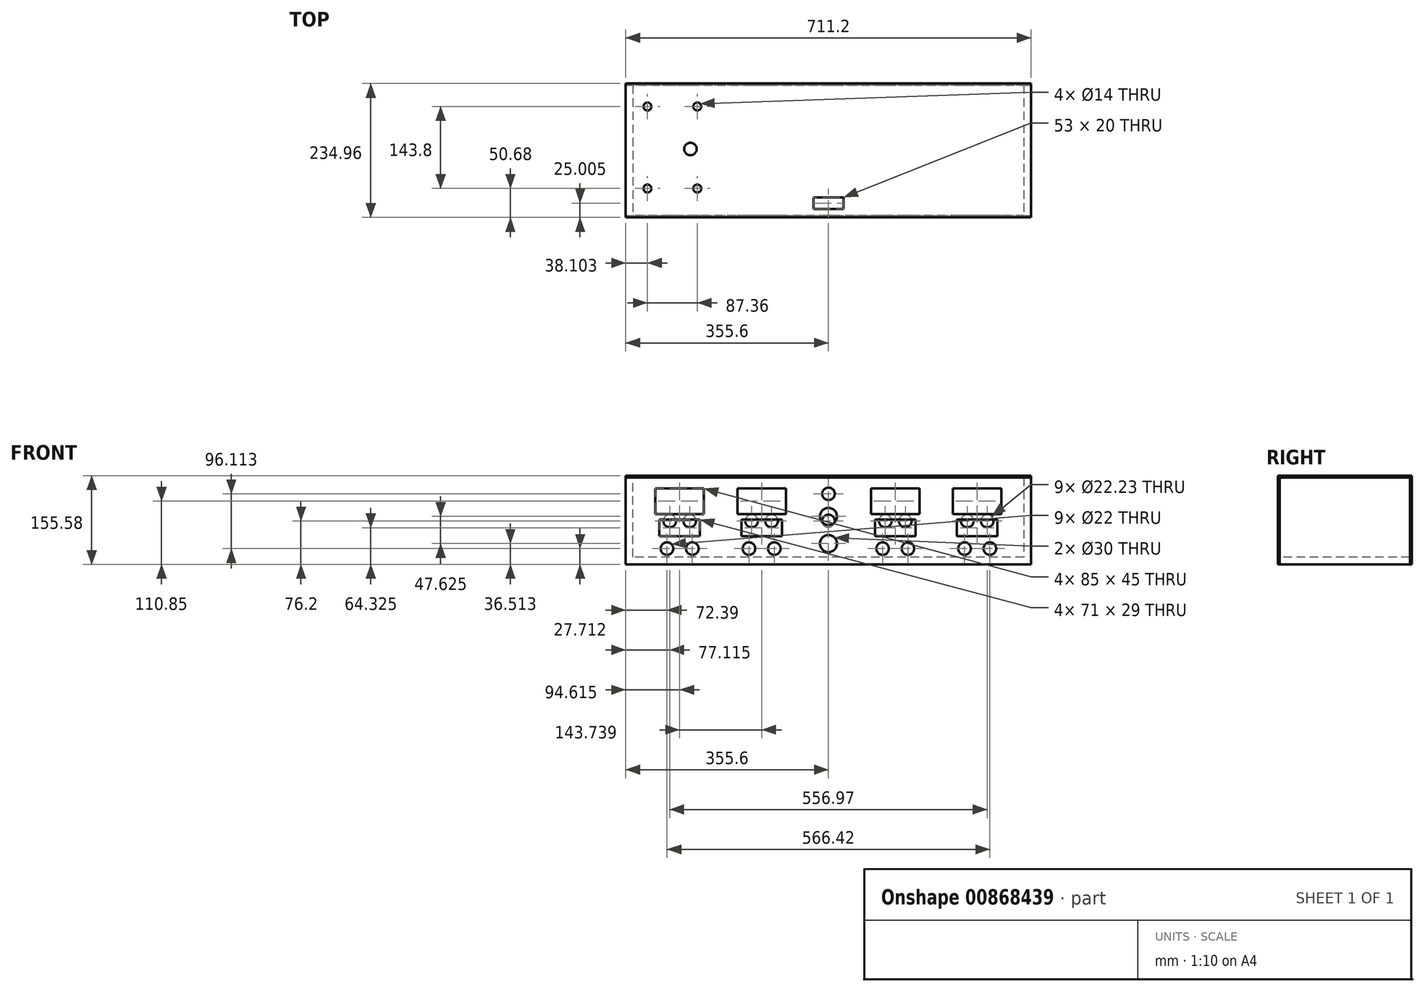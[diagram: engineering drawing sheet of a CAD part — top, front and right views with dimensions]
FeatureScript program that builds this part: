
annotation { "Feature Type Name" : "Feature", "Feature Type Description" : "" }
export const myFeature = defineFeature(function(context is Context, id is Id, definition is map)
    precondition{}
    {
        {
            var Q0;
            Q0=qCreatedBy(makeId("Front.planeOp"),FACE);
            var sketch = newSketch(context, id + "F0", { "sketchPlane" : qUnion([Q0])});
            skLineSegment(sketch, "E0.bottom", {"start": v(0, 0) * mm, "end": v(711.2, 0) * mm});
            skLineSegment(sketch, "E0.top", {"start": v(0, 152.4) * mm, "end": v(711.2, 152.4) * mm});
            skLineSegment(sketch, "E0.left", {"start": v(0, 0) * mm, "end": v(0, 152.4) * mm});
            skLineSegment(sketch, "E0.right", {"start": v(711.2, 0) * mm, "end": v(711.2, 152.4) * mm});
            skLineSegment(sketch, "E1.bottom", {"start": v(52.11, 133.35) * mm, "end": v(137.11, 133.35) * mm});
            skLineSegment(sketch, "E1.top", {"start": v(52.11, 88.35) * mm, "end": v(137.11, 88.35) * mm});
            skLineSegment(sketch, "E1.left", {"start": v(52.11, 133.35) * mm, "end": v(52.11, 88.35) * mm});
            skLineSegment(sketch, "E1.right", {"start": v(137.11, 133.35) * mm, "end": v(137.11, 88.35) * mm});
            skLineSegment(sketch, "E2.bottom", {"start": v(59.11, 78.83) * mm, "end": v(130.11, 78.83) * mm});
            skLineSegment(sketch, "E2.top", {"start": v(59.11, 49.83) * mm, "end": v(130.11, 49.83) * mm});
            skLineSegment(sketch, "E2.left", {"start": v(59.11, 78.83) * mm, "end": v(59.11, 49.83) * mm});
            skLineSegment(sketch, "E2.right", {"start": v(130.11, 78.83) * mm, "end": v(130.11, 49.83) * mm});
            skPoint(sketch, "E3", {"position": v(94.61, 133.35) * mm});
            skPoint(sketch, "E4", {"position": v(94.61, 88.35) * mm});
            skPoint(sketch, "E5", {"position": v(94.61, 78.83) * mm});
            skPoint(sketch, "E6", {"position": v(94.61, 49.83) * mm});
            skLineSegment(sketch, "E7", {"start": v(0, 139.7) * mm, "end": v(711.2, 139.7) * mm, "construction": true});
            skLineSegment(sketch, "E8", {"start": v(711.2, 12.7) * mm, "end": v(0, 12.7) * mm});
            skLineSegment(sketch, "E9", {"start": v(12.7, 0) * mm, "end": v(12.7, 152.4) * mm});
            skLineSegment(sketch, "E10", {"start": v(698.5, 152.4) * mm, "end": v(698.5, 0) * mm});
            skLineSegment(sketch, "E11", {"start": v(94.61, 139.7) * mm, "end": v(94.61, 12.7) * mm, "construction": true});
            skCircle(sketch, "E12", {"center": v(72.39, 27.71) * mm, "radius": 11 * mm});
            skCircle(sketch, "E13", {"center": v(116.84, 27.71) * mm, "radius": 11 * mm});
            skLineSegment(sketch, "E14", {"start": v(72.39, 27.71) * mm, "end": v(116.84, 27.71) * mm, "construction": true});
            skPoint(sketch, "E15", {"position": v(94.61, 27.71) * mm});
            skLineSegment(sketch, "E16.0", {"start": v(49.11, 136.35) * mm, "end": v(49.11, 85.35) * mm, "construction": true});
            skLineSegment(sketch, "E16.1", {"start": v(49.12, 136.35) * mm, "end": v(140.11, 136.35) * mm, "construction": true});
            skLineSegment(sketch, "E16.2", {"start": v(140.12, 136.35) * mm, "end": v(140.11, 85.35) * mm, "construction": true});
            skLineSegment(sketch, "E16.3", {"start": v(49.11, 85.35) * mm, "end": v(140.11, 85.35) * mm, "construction": true});
            skLineSegment(sketch, "E17.0", {"start": v(55.11, 82.83) * mm, "end": v(134.11, 82.83) * mm, "construction": true});
            skLineSegment(sketch, "E17.1", {"start": v(55.11, 82.83) * mm, "end": v(55.11, 45.83) * mm, "construction": true});
            skLineSegment(sketch, "E17.2", {"start": v(55.11, 45.83) * mm, "end": v(134.11, 45.83) * mm, "construction": true});
            skLineSegment(sketch, "E17.3", {"start": v(134.11, 82.83) * mm, "end": v(134.11, 45.83) * mm, "construction": true});
            skCircle(sketch, "E18.0", {"center": v(72.39, 27.71) * mm, "radius": 15 * mm, "construction": true});
            skCircle(sketch, "E19.0", {"center": v(116.84, 27.71) * mm, "radius": 15 * mm, "construction": true});
            skLineSegment(sketch, "E20", {"start": v(616.59, 139.7) * mm, "end": v(616.59, 12.7) * mm, "construction": true});
            skLineSegment(sketch, "E21", {"start": v(355.6, 139.7) * mm, "end": v(355.6, 12.7) * mm, "construction": true});
            skLineSegment(sketch, "E22", {"start": v(238.35, 139.7) * mm, "end": v(238.35, 12.7) * mm, "construction": true});
            skLineSegment(sketch, "E23", {"start": v(472.85, 139.7) * mm, "end": v(472.85, 12.7) * mm, "construction": true});
            skLineSegment(sketch, "E24", {"start": v(166.48, 152.4) * mm, "end": v(166.48, 0) * mm, "construction": true});
            skLineSegment(sketch, "E25", {"start": v(544.72, 152.4) * mm, "end": v(544.72, 0) * mm, "construction": true});
            skLineSegment(sketch, "E26.MirrorCS", {"start": v(280.85, 133.35) * mm, "end": v(195.85, 133.35) * mm});
            skLineSegment(sketch, "E27.MirrorCS", {"start": v(192.85, 136.35) * mm, "end": v(192.85, 85.35) * mm, "construction": true});
            skLineSegment(sketch, "E28.MirrorCS", {"start": v(280.85, 133.35) * mm, "end": v(280.85, 88.35) * mm});
            skLineSegment(sketch, "E29.MirrorCS", {"start": v(277.85, 82.83) * mm, "end": v(277.85, 45.83) * mm, "construction": true});
            skLineSegment(sketch, "E30.MirrorCS", {"start": v(273.85, 78.83) * mm, "end": v(202.85, 78.83) * mm});
            skLineSegment(sketch, "E31.MirrorCS", {"start": v(280.85, 88.35) * mm, "end": v(195.85, 88.35) * mm});
            skLineSegment(sketch, "E32.MirrorCS", {"start": v(260.58, 27.71) * mm, "end": v(216.13, 27.71) * mm, "construction": true});
            skPoint(sketch, "E33.MirrorP", {"position": v(238.35, 27.71) * mm});
            skLineSegment(sketch, "E34.MirrorCS", {"start": v(195.85, 133.35) * mm, "end": v(195.85, 88.35) * mm});
            skCircle(sketch, "E35.MirrorC", {"center": v(216.13, 27.71) * mm, "radius": 11 * mm});
            skLineSegment(sketch, "E36.MirrorCS", {"start": v(283.85, 85.35) * mm, "end": v(192.85, 85.35) * mm, "construction": true});
            skPoint(sketch, "E37.MirrorP", {"position": v(238.35, 133.35) * mm});
            skCircle(sketch, "E38.MirrorC", {"center": v(260.58, 27.71) * mm, "radius": 11 * mm});
            skLineSegment(sketch, "E39.MirrorCS", {"start": v(273.85, 49.83) * mm, "end": v(202.85, 49.83) * mm});
            skLineSegment(sketch, "E40.MirrorCS", {"start": v(277.85, 45.83) * mm, "end": v(198.85, 45.83) * mm, "construction": true});
            skPoint(sketch, "E41.MirrorP", {"position": v(238.35, 78.83) * mm});
            skPoint(sketch, "E42.MirrorP", {"position": v(238.35, 49.83) * mm});
            skLineSegment(sketch, "E43.MirrorCS", {"start": v(273.85, 78.83) * mm, "end": v(273.85, 49.83) * mm});
            skPoint(sketch, "E44.MirrorP", {"position": v(238.35, 88.35) * mm});
            skLineSegment(sketch, "E45.MirrorCS", {"start": v(198.85, 82.83) * mm, "end": v(198.85, 45.83) * mm, "construction": true});
            skLineSegment(sketch, "E46.MirrorCS", {"start": v(277.85, 82.83) * mm, "end": v(198.85, 82.83) * mm, "construction": true});
            skLineSegment(sketch, "E47.MirrorCS", {"start": v(283.85, 136.35) * mm, "end": v(192.85, 136.35) * mm, "construction": true});
            skLineSegment(sketch, "E48.MirrorCS", {"start": v(283.85, 136.35) * mm, "end": v(283.85, 85.35) * mm, "construction": true});
            skLineSegment(sketch, "E49.MirrorCS", {"start": v(202.85, 78.83) * mm, "end": v(202.85, 49.83) * mm});
            skCircle(sketch, "E50.MirrorC", {"center": v(216.13, 27.71) * mm, "radius": 15 * mm, "construction": true});
            skCircle(sketch, "E51.MirrorC", {"center": v(260.58, 27.71) * mm, "radius": 15 * mm, "construction": true});
            skLineSegment(sketch, "E52.MirrorCS", {"start": v(430.35, 88.35) * mm, "end": v(515.35, 88.35) * mm});
            skLineSegment(sketch, "E53.MirrorCS", {"start": v(518.35, 136.35) * mm, "end": v(518.35, 85.35) * mm, "construction": true});
            skLineSegment(sketch, "E54.MirrorCS", {"start": v(656.09, 45.83) * mm, "end": v(577.09, 45.83) * mm, "construction": true});
            skLineSegment(sketch, "E55.MirrorCS", {"start": v(515.35, 133.35) * mm, "end": v(515.35, 88.35) * mm});
            skLineSegment(sketch, "E56.MirrorCS", {"start": v(656.09, 82.83) * mm, "end": v(656.09, 45.83) * mm, "construction": true});
            skCircle(sketch, "E57.MirrorC", {"center": v(450.62, 27.71) * mm, "radius": 11 * mm});
            skPoint(sketch, "E58.MirrorP", {"position": v(472.85, 88.35) * mm});
            skPoint(sketch, "E59.MirrorP", {"position": v(616.59, 78.83) * mm});
            skLineSegment(sketch, "E60.MirrorCS", {"start": v(574.09, 133.35) * mm, "end": v(574.09, 88.35) * mm});
            skLineSegment(sketch, "E61.MirrorCS", {"start": v(433.35, 82.83) * mm, "end": v(512.35, 82.83) * mm, "construction": true});
            skLineSegment(sketch, "E62.MirrorCS", {"start": v(662.09, 136.35) * mm, "end": v(571.09, 136.35) * mm, "construction": true});
            skLineSegment(sketch, "E63.MirrorCS", {"start": v(437.35, 49.83) * mm, "end": v(508.35, 49.83) * mm});
            skPoint(sketch, "E64.MirrorP", {"position": v(472.85, 133.35) * mm});
            skLineSegment(sketch, "E65.MirrorCS", {"start": v(427.35, 136.35) * mm, "end": v(518.35, 136.35) * mm, "construction": true});
            skLineSegment(sketch, "E66.MirrorCS", {"start": v(659.09, 88.35) * mm, "end": v(574.09, 88.35) * mm});
            skLineSegment(sketch, "E67.MirrorCS", {"start": v(430.35, 133.35) * mm, "end": v(515.35, 133.35) * mm});
            skLineSegment(sketch, "E68.MirrorCS", {"start": v(662.09, 85.35) * mm, "end": v(571.09, 85.35) * mm, "construction": true});
            skCircle(sketch, "E69.MirrorC", {"center": v(638.81, 27.71) * mm, "radius": 11 * mm});
            skLineSegment(sketch, "E70.MirrorCS", {"start": v(659.09, 133.35) * mm, "end": v(659.09, 88.35) * mm});
            skCircle(sketch, "E71.MirrorC", {"center": v(495.07, 27.71) * mm, "radius": 11 * mm});
            skPoint(sketch, "E72.MirrorP", {"position": v(616.59, 88.35) * mm});
            skLineSegment(sketch, "E73.MirrorCS", {"start": v(430.35, 133.35) * mm, "end": v(430.35, 88.35) * mm});
            skLineSegment(sketch, "E74.MirrorCS", {"start": v(659.09, 133.35) * mm, "end": v(574.09, 133.35) * mm});
            skLineSegment(sketch, "E75.MirrorCS", {"start": v(437.35, 78.83) * mm, "end": v(437.35, 49.83) * mm});
            skLineSegment(sketch, "E76.MirrorCS", {"start": v(433.35, 82.83) * mm, "end": v(433.35, 45.83) * mm, "construction": true});
            skLineSegment(sketch, "E77.MirrorCS", {"start": v(427.35, 85.35) * mm, "end": v(518.35, 85.35) * mm, "construction": true});
            skLineSegment(sketch, "E78.MirrorCS", {"start": v(656.09, 82.83) * mm, "end": v(577.09, 82.83) * mm, "construction": true});
            skLineSegment(sketch, "E79.MirrorCS", {"start": v(427.35, 136.35) * mm, "end": v(427.35, 85.35) * mm, "construction": true});
            skLineSegment(sketch, "E80.MirrorCS", {"start": v(450.62, 27.71) * mm, "end": v(495.07, 27.71) * mm, "construction": true});
            skCircle(sketch, "E81.MirrorC", {"center": v(594.36, 27.71) * mm, "radius": 11 * mm});
            skLineSegment(sketch, "E82.MirrorCS", {"start": v(662.09, 136.35) * mm, "end": v(662.09, 85.35) * mm, "construction": true});
            skPoint(sketch, "E83.MirrorP", {"position": v(616.59, 133.35) * mm});
            skLineSegment(sketch, "E84.MirrorCS", {"start": v(652.09, 78.83) * mm, "end": v(652.09, 49.83) * mm});
            skLineSegment(sketch, "E85.MirrorCS", {"start": v(652.09, 49.83) * mm, "end": v(581.09, 49.83) * mm});
            skLineSegment(sketch, "E86.MirrorCS", {"start": v(577.09, 82.83) * mm, "end": v(577.09, 45.83) * mm, "construction": true});
            skPoint(sketch, "E87.MirrorP", {"position": v(472.85, 49.83) * mm});
            skLineSegment(sketch, "E88.MirrorCS", {"start": v(652.09, 78.83) * mm, "end": v(581.09, 78.83) * mm});
            skPoint(sketch, "E89.MirrorP", {"position": v(616.59, 49.83) * mm});
            skPoint(sketch, "E90.MirrorP", {"position": v(616.59, 27.71) * mm});
            skLineSegment(sketch, "E91.MirrorCS", {"start": v(512.35, 82.83) * mm, "end": v(512.35, 45.83) * mm, "construction": true});
            skLineSegment(sketch, "E92.MirrorCS", {"start": v(571.09, 136.35) * mm, "end": v(571.09, 85.35) * mm, "construction": true});
            skPoint(sketch, "E93.MirrorP", {"position": v(472.85, 78.83) * mm});
            skLineSegment(sketch, "E94.MirrorCS", {"start": v(508.35, 78.83) * mm, "end": v(508.35, 49.83) * mm});
            skLineSegment(sketch, "E95.MirrorCS", {"start": v(581.09, 78.83) * mm, "end": v(581.09, 49.83) * mm});
            skPoint(sketch, "E96.MirrorP", {"position": v(472.85, 27.71) * mm});
            skLineSegment(sketch, "E97.MirrorCS", {"start": v(437.35, 78.83) * mm, "end": v(508.35, 78.83) * mm});
            skLineSegment(sketch, "E98.MirrorCS", {"start": v(638.81, 27.71) * mm, "end": v(594.36, 27.71) * mm, "construction": true});
            skLineSegment(sketch, "E99.MirrorCS", {"start": v(433.35, 45.83) * mm, "end": v(512.35, 45.83) * mm, "construction": true});
            skCircle(sketch, "E100.MirrorC", {"center": v(450.62, 27.71) * mm, "radius": 15 * mm, "construction": true});
            skCircle(sketch, "E101.MirrorC", {"center": v(495.07, 27.71) * mm, "radius": 15 * mm, "construction": true});
            skCircle(sketch, "E102.MirrorC", {"center": v(594.36, 27.71) * mm, "radius": 15 * mm, "construction": true});
            skCircle(sketch, "E103.MirrorC", {"center": v(638.81, 27.71) * mm, "radius": 15 * mm, "construction": true});
            skCircle(sketch, "E104", {"center": v(355.6, 36.51) * mm, "radius": 15 * mm});
            skCircle(sketch, "E105", {"center": v(355.6, 84.14) * mm, "radius": 15 * mm});
            skCircle(sketch, "E106", {"center": v(355.6, 123.83) * mm, "radius": 11 * mm});
            skCircle(sketch, "E107", {"center": v(355.6, 123.83) * mm, "radius": 15 * mm, "construction": true});
            skLineSegment(sketch, "E108.bottom", {"start": v(376.94, 57.85) * mm, "end": v(334.26, 57.85) * mm, "construction": true});
            skLineSegment(sketch, "E108.top", {"start": v(376.94, 15.18) * mm, "end": v(334.26, 15.18) * mm, "construction": true});
            skLineSegment(sketch, "E108.left", {"start": v(376.94, 57.85) * mm, "end": v(376.94, 15.18) * mm, "construction": true});
            skLineSegment(sketch, "E108.right", {"start": v(334.26, 57.85) * mm, "end": v(334.26, 15.18) * mm, "construction": true});
            skLineSegment(sketch, "E109.bottom", {"start": v(334.26, 105.47) * mm, "end": v(376.94, 105.47) * mm, "construction": true});
            skLineSegment(sketch, "E109.top", {"start": v(334.26, 62.8) * mm, "end": v(376.94, 62.8) * mm, "construction": true});
            skLineSegment(sketch, "E109.left", {"start": v(334.26, 105.47) * mm, "end": v(334.26, 62.8) * mm, "construction": true});
            skLineSegment(sketch, "E109.right", {"start": v(376.94, 105.47) * mm, "end": v(376.94, 62.8) * mm, "construction": true});
            skSolve(sketch);
        }
        {
            var Q0;
            Q0=makeQuery(id+"F0.imprint","IMPRINT",FACE,{"disambiguationData":[TD([[makeQuery(id+"F0.imprint","IMPRINT",EDGE,{"derivedFrom":sQuery(id+"F0.wireOp",EDGE,"E0.bottom")}),1.0]])]});
            var Q1;
            {var subQ0=sQuery(id+"F0.wireOp",EDGE,"E0.left");var subQ1=sQuery(id+"F0.wireOp",EDGE,"E0.top");var subQ2=makeQuery(id+"F0.imprint","INTERSECT",VERTEX,{"derivedFrom":[subQ1,subQ0]});Q1=makeQuery(id+"F0.imprint","IMPRINT",FACE,{"disambiguationData":[TD([[makeQuery(id+"F0.imprint","IMPRINT",EDGE,{"disambiguationData":[TD([[subQ2,-1.0]])],"derivedFrom":subQ1}),-1.0]])]});}
            var Q2;
            Q2=makeQuery(id+"F0.imprint","IMPRINT",FACE,{"disambiguationData":[TD([[makeQuery(id+"F0.imprint","IMPRINT",EDGE,{"derivedFrom":sQuery(id+"F0.wireOp",EDGE,"E1.bottom")}),1.0]])]});
            var Q3;
            {var subQ0=sQuery(id+"F0.wireOp",EDGE,"E0.right");var subQ1=sQuery(id+"F0.wireOp",EDGE,"E0.top");var subQ2=makeQuery(id+"F0.imprint","INTERSECT",VERTEX,{"derivedFrom":[subQ1,subQ0]});Q3=makeQuery(id+"F0.imprint","IMPRINT",FACE,{"disambiguationData":[TD([[makeQuery(id+"F0.imprint","IMPRINT",EDGE,{"disambiguationData":[TD([[subQ2,1.0]])],"derivedFrom":subQ1}),-1.0]])]});}
            extrude(context, id + "F1", {"entities" : qUnion([Q0, Q1, Q2, Q3]), "depth" : 3.17 * mm, "offsetDistance" : 25 * mm});
        }
        {
            var Q0;
            {var subQ0=sQuery(id+"F0.wireOp",EDGE,"E9");var subQ1=sQuery(id+"F0.wireOp",EDGE,"E0.bottom");var subQ2=makeQuery(id+"F0.imprint","INTERSECT",VERTEX,{"derivedFrom":[subQ1,subQ0]});Q0=makeQuery(id+"F0.imprint","IMPRINT",FACE,{"disambiguationData":[TD([[makeQuery(id+"F0.imprint","IMPRINT",EDGE,{"disambiguationData":[TD([[subQ2,-1.0]])],"derivedFrom":subQ1}),1.0]])]});}
            var Q1;
            {var subQ0=sQuery(id+"F0.wireOp",EDGE,"E0.left");var subQ1=sQuery(id+"F0.wireOp",EDGE,"E0.bottom");var subQ2=makeQuery(id+"F0.imprint","INTERSECT",VERTEX,{"derivedFrom":[subQ1,subQ0]});Q1=makeQuery(id+"F0.imprint","IMPRINT",FACE,{"disambiguationData":[TD([[makeQuery(id+"F0.imprint","IMPRINT",EDGE,{"disambiguationData":[TD([[subQ2,-1.0]])],"derivedFrom":subQ1}),1.0]])]});}
            var Q2;
            {var subQ0=sQuery(id+"F0.wireOp",EDGE,"E0.right");var subQ1=sQuery(id+"F0.wireOp",EDGE,"E0.bottom");var subQ2=makeQuery(id+"F0.imprint","INTERSECT",VERTEX,{"derivedFrom":[subQ1,subQ0]});Q2=makeQuery(id+"F0.imprint","IMPRINT",FACE,{"disambiguationData":[TD([[makeQuery(id+"F0.imprint","IMPRINT",EDGE,{"disambiguationData":[TD([[subQ2,1.0]])],"derivedFrom":subQ1}),1.0]])]});}
            var Q3;
            {var subQ0=sQuery(id+"F0.wireOp",EDGE,"E0.left");var subQ1=sQuery(id+"F0.wireOp",EDGE,"E0.top");var subQ2=makeQuery(id+"F0.imprint","INTERSECT",VERTEX,{"derivedFrom":[subQ1,subQ0]});Q3=makeQuery(id+"F0.imprint","IMPRINT",FACE,{"disambiguationData":[TD([[makeQuery(id+"F0.imprint","IMPRINT",EDGE,{"disambiguationData":[TD([[subQ2,-1.0]])],"derivedFrom":subQ1}),-1.0]])]});}
            var Q4;
            {var subQ0=sQuery(id+"F0.wireOp",EDGE,"E0.right");var subQ1=sQuery(id+"F0.wireOp",EDGE,"E0.top");var subQ2=makeQuery(id+"F0.imprint","INTERSECT",VERTEX,{"derivedFrom":[subQ1,subQ0]});Q4=makeQuery(id+"F0.imprint","IMPRINT",FACE,{"disambiguationData":[TD([[makeQuery(id+"F0.imprint","IMPRINT",EDGE,{"disambiguationData":[TD([[subQ2,1.0]])],"derivedFrom":subQ1}),-1.0]])]});}
            extrude(context, id + "F2", {"entities" : qUnion([Q0, Q1, Q2, Q3, Q4]), "oppositeDirection" : true, "depth" : 228.6 * mm, "offsetDistance" : 25 * mm});
        }
        {
            var Q0;
            Q0=makeQuery(id+"F2.opExtrude","CAP_FACE",FACE,{"disambiguationData":[OSD([sQuery(id+"F0.wireOp",EDGE,"E0.bottom"),sQuery(id+"F0.wireOp",EDGE,"E0.top"),sQuery(id+"F0.wireOp",EDGE,"E0.left"),sQuery(id+"F0.wireOp",EDGE,"E0.right"),sQuery(id+"F0.wireOp",EDGE,"E8"),sQuery(id+"F0.wireOp",EDGE,"E9"),sQuery(id+"F0.wireOp",EDGE,"E10")])],"isStart":false});
            var sketch = newSketch(context, id + "F3", { "sketchPlane" : qUnion([Q0])});
            skLineSegment(sketch, "E110.0", {"start": v(-711.2, 0) * mm, "end": v(-711.2, 152.4) * mm});
            skLineSegment(sketch, "E111.0", {"start": v(0, 0) * mm, "end": v(-711.2, 0) * mm});
            skLineSegment(sketch, "E112.0", {"start": v(0, 0) * mm, "end": v(0, 152.4) * mm});
            skLineSegment(sketch, "E113.0", {"start": v(0, 152.4) * mm, "end": v(-711.2, 152.4) * mm});
            skLineSegment(sketch, "E114.0", {"start": v(-616.59, 139.7) * mm, "end": v(-616.59, 12.7) * mm, "construction": true});
            skLineSegment(sketch, "E115.0", {"start": v(-472.85, 139.7) * mm, "end": v(-472.85, 12.7) * mm, "construction": true});
            skLineSegment(sketch, "E116.0", {"start": v(-355.6, 139.7) * mm, "end": v(-355.6, 12.7) * mm, "construction": true});
            skLineSegment(sketch, "E117.0", {"start": v(-238.35, 139.7) * mm, "end": v(-238.35, 12.7) * mm, "construction": true});
            skLineSegment(sketch, "E118.0", {"start": v(-94.61, 139.7) * mm, "end": v(-94.61, 12.7) * mm, "construction": true});
            skLineSegment(sketch, "E119.0", {"start": v(-711.2, 12.7) * mm, "end": v(0, 12.7) * mm, "construction": true});
            skLineSegment(sketch, "E120.0", {"start": v(-12.7, 0) * mm, "end": v(-12.7, 152.4) * mm, "construction": true});
            skLineSegment(sketch, "E121.0", {"start": v(-698.5, 152.4) * mm, "end": v(-698.5, 0) * mm, "construction": true});
            skLineSegment(sketch, "E122", {"start": v(-711.2, 76.2) * mm, "end": v(0, 76.2) * mm, "construction": true});
            skCircle(sketch, "E123", {"center": v(-634.09, 76.2) * mm, "radius": 11.11 * mm});
            skCircle(sketch, "E124.MirrorC", {"center": v(-599.09, 76.2) * mm, "radius": 11.11 * mm});
            skLineSegment(sketch, "E125.0", {"start": v(-544.72, 152.4) * mm, "end": v(-544.72, 0) * mm, "construction": true});
            skLineSegment(sketch, "E126.0", {"start": v(-166.48, 152.4) * mm, "end": v(-166.48, 0) * mm, "construction": true});
            skCircle(sketch, "E127.MirrorC", {"center": v(-490.35, 76.2) * mm, "radius": 11.11 * mm});
            skCircle(sketch, "E128.MirrorC", {"center": v(-455.35, 76.2) * mm, "radius": 11.11 * mm});
            skCircle(sketch, "E129.MirrorC", {"center": v(-77.12, 76.2) * mm, "radius": 11.11 * mm});
            skCircle(sketch, "E130.MirrorC", {"center": v(-112.11, 76.2) * mm, "radius": 11.11 * mm});
            skCircle(sketch, "E131.MirrorC", {"center": v(-220.85, 76.2) * mm, "radius": 11.11 * mm});
            skCircle(sketch, "E132.MirrorC", {"center": v(-255.85, 76.2) * mm, "radius": 11.11 * mm});
            skCircle(sketch, "E133", {"center": v(-355.6, 76.2) * mm, "radius": 11.11 * mm});
            skSolve(sketch);
        }
        {
            var Q0;
            {var subQ3=sQuery(id+"F3.wireOp",EDGE,"E110.0");Q0=makeQuery(id+"F3.imprint","IMPRINT",FACE,{"disambiguationData":[TD([[makeQuery(id+"F3.imprint","IMPRINT",EDGE,{"derivedFrom":subQ3}),-1.0]])]});}
            var Q1;
            Q1=makeQuery(id+"F3.imprint","IMPRINT",FACE,{"disambiguationData":[TD([[makeQuery(id+"F3.imprint","IMPRINT",EDGE,{"derivedFrom":sQuery(id+"F3.wireOp",EDGE,"E123")}),-1.0]])]});
            extrude(context, id + "F4", {"entities" : qUnion([Q0, Q1]), "depth" : 3.17 * mm, "offsetDistance" : 25 * mm});
        }
        {
            var Q0;
            {var subQ0=sQuery(id+"F0.wireOp",EDGE,"E0.top");Q0=makeQuery(id+"F2.opExtrude","SWEPT_FACE",FACE,{"disambiguationData":[OSD([subQ0]),TDD([makeQuery(id+"F0.imprint","IMPRINT",EDGE,{"disambiguationData":[TD([[makeQuery(id+"F0.imprint","INTERSECT",VERTEX,{"derivedFrom":[subQ0,sQuery(id+"F0.wireOp",EDGE,"E0.left")]}),-1.0]])],"derivedFrom":subQ0})])]});}
            var sketch = newSketch(context, id + "F5", { "sketchPlane" : qUnion([Q0])});
            skLineSegment(sketch, "E134.0.0", {"start": v(0, 0) * mm, "end": v(12.7, 0) * mm});
            skLineSegment(sketch, "E134.0.1", {"start": v(12.7, 0) * mm, "end": v(12.7, 228.6) * mm, "construction": true});
            skLineSegment(sketch, "E134.0.2", {"start": v(12.7, 228.6) * mm, "end": v(0, 228.6) * mm});
            skLineSegment(sketch, "E134.0.3", {"start": v(0, 228.6) * mm, "end": v(0, 0) * mm});
            skLineSegment(sketch, "E135.0.0", {"start": v(698.5, 0) * mm, "end": v(711.2, 0) * mm});
            skLineSegment(sketch, "E135.0.1", {"start": v(711.2, 0) * mm, "end": v(711.2, 228.6) * mm});
            skLineSegment(sketch, "E135.0.2", {"start": v(711.2, 228.6) * mm, "end": v(698.5, 228.6) * mm});
            skLineSegment(sketch, "E135.0.3", {"start": v(698.5, 228.6) * mm, "end": v(698.5, 0) * mm, "construction": true});
            skLineSegment(sketch, "E136.0.0", {"start": v(0, 228.6) * mm, "end": v(711.2, 228.6) * mm, "construction": true});
            skLineSegment(sketch, "E136.0.1", {"start": v(711.2, 228.6) * mm, "end": v(711.2, 231.78) * mm});
            skLineSegment(sketch, "E136.0.2", {"start": v(711.2, 231.78) * mm, "end": v(0, 231.78) * mm});
            skLineSegment(sketch, "E136.0.3", {"start": v(0, 231.78) * mm, "end": v(0, 228.6) * mm});
            skLineSegment(sketch, "E137.0.0", {"start": v(711.2, 0) * mm, "end": v(0, 0) * mm, "construction": true});
            skLineSegment(sketch, "E137.0.1", {"start": v(0, 0) * mm, "end": v(0, -3.18) * mm});
            skLineSegment(sketch, "E137.0.2", {"start": v(0, -3.18) * mm, "end": v(711.2, -3.18) * mm});
            skLineSegment(sketch, "E137.0.3", {"start": v(711.2, -3.18) * mm, "end": v(711.2, 0) * mm});
            skLineSegment(sketch, "E138", {"start": v(0, 114.3) * mm, "end": v(711.2, 114.3) * mm, "construction": true});
            skLineSegment(sketch, "E139", {"start": v(159.1, 201.8) * mm, "end": v(159.1, 26.8) * mm, "construction": true});
            skLineSegment(sketch, "E140", {"start": v(159.1, 26.8) * mm, "end": v(228.1, 26.8) * mm, "construction": true});
            skLineSegment(sketch, "E141", {"start": v(228.1, 59.8) * mm, "end": v(228.1, 26.8) * mm, "construction": true});
            skLineSegment(sketch, "E142", {"start": v(228.1, 59.8) * mm, "end": v(309.1, 59.8) * mm, "construction": true});
            skLineSegment(sketch, "E143", {"start": v(309.1, 59.8) * mm, "end": v(309.1, 201.8) * mm, "construction": true});
            skLineSegment(sketch, "E144", {"start": v(309.1, 201.8) * mm, "end": v(159.1, 201.8) * mm, "construction": true});
            skCircle(sketch, "E145", {"center": v(173.1, 184.8) * mm, "radius": 4 * mm, "construction": true});
            skCircle(sketch, "E146", {"center": v(295.1, 184.8) * mm, "radius": 4 * mm, "construction": true});
            skCircle(sketch, "E147", {"center": v(173.1, 44.8) * mm, "radius": 4 * mm, "construction": true});
            skCircle(sketch, "E148", {"center": v(295.1, 74.8) * mm, "radius": 4 * mm, "construction": true});
            skPoint(sketch, "E149", {"position": v(159.1, 114.3) * mm});
            skLineSegment(sketch, "E150.bottom", {"start": v(329.1, 174.3) * mm, "end": v(478.1, 174.3) * mm, "construction": true});
            skLineSegment(sketch, "E150.top", {"start": v(329.1, 54.3) * mm, "end": v(478.1, 54.3) * mm, "construction": true});
            skLineSegment(sketch, "E150.left", {"start": v(329.1, 174.3) * mm, "end": v(329.1, 54.3) * mm, "construction": true});
            skLineSegment(sketch, "E150.right", {"start": v(478.1, 174.3) * mm, "end": v(478.1, 54.3) * mm, "construction": true});
            skPoint(sketch, "E151", {"position": v(329.1, 114.3) * mm});
            skCircle(sketch, "E152", {"center": v(346.1, 158.3) * mm, "radius": 3.5 * mm, "construction": true});
            skCircle(sketch, "E153", {"center": v(461.1, 158.3) * mm, "radius": 3.5 * mm, "construction": true});
            skCircle(sketch, "E154", {"center": v(461.1, 68.3) * mm, "radius": 3.5 * mm, "construction": true});
            skCircle(sketch, "E155", {"center": v(346.1, 68.3) * mm, "radius": 3.5 * mm, "construction": true});
            skLineSegment(sketch, "E156.bottom", {"start": v(498.1, 191.8) * mm, "end": v(686.1, 191.8) * mm, "construction": true});
            skLineSegment(sketch, "E156.top", {"start": v(498.1, 36.8) * mm, "end": v(686.1, 36.8) * mm, "construction": true});
            skLineSegment(sketch, "E156.left", {"start": v(498.1, 191.8) * mm, "end": v(498.1, 36.8) * mm, "construction": true});
            skLineSegment(sketch, "E156.right", {"start": v(686.1, 191.8) * mm, "end": v(686.1, 36.8) * mm, "construction": true});
            skPoint(sketch, "E157", {"position": v(498.1, 114.3) * mm});
            skCircle(sketch, "E158", {"center": v(513.1, 177.8) * mm, "radius": 4 * mm, "construction": true});
            skCircle(sketch, "E159", {"center": v(673.1, 177.8) * mm, "radius": 4 * mm, "construction": true});
            skCircle(sketch, "E160", {"center": v(673.1, 51.8) * mm, "radius": 4 * mm, "construction": true});
            skCircle(sketch, "E161", {"center": v(513.1, 51.8) * mm, "radius": 4 * mm, "construction": true});
            skLineSegment(sketch, "E162", {"start": v(498.1, 186.8) * mm, "end": v(513.1, 186.8) * mm, "construction": true});
            skLineSegment(sketch, "E163", {"start": v(513.1, 168.8) * mm, "end": v(498.1, 168.8) * mm, "construction": true});
            skArc(sketch, "E164", {"start": v(513.1, 186.8) * mm, "mid": v(504.1, 177.8) * mm, "end": v(513.1, 168.8) * mm, "construction": true});
            skArc(sketch, "E165", {"start": v(513.1, 168.8) * mm, "mid": v(522.1, 177.8) * mm, "end": v(513.1, 186.8) * mm, "construction": true});
            skLineSegment(sketch, "E166", {"start": v(513.1, 60.8) * mm, "end": v(498.1, 60.8) * mm, "construction": true});
            skLineSegment(sketch, "E167", {"start": v(513.1, 42.8) * mm, "end": v(498.1, 42.8) * mm, "construction": true});
            skLineSegment(sketch, "E168", {"start": v(673.1, 60.8) * mm, "end": v(686.1, 60.8) * mm, "construction": true});
            skLineSegment(sketch, "E169", {"start": v(673.1, 42.8) * mm, "end": v(686.1, 42.8) * mm, "construction": true});
            skLineSegment(sketch, "E170", {"start": v(673.1, 186.8) * mm, "end": v(686.1, 186.8) * mm, "construction": true});
            skLineSegment(sketch, "E171", {"start": v(673.1, 168.8) * mm, "end": v(686.1, 168.8) * mm, "construction": true});
            skArc(sketch, "E172", {"start": v(673.1, 186.8) * mm, "mid": v(664.1, 177.8) * mm, "end": v(673.1, 168.8) * mm, "construction": true});
            skArc(sketch, "E173", {"start": v(673.1, 168.8) * mm, "mid": v(682.1, 177.8) * mm, "end": v(673.1, 186.8) * mm, "construction": true});
            skArc(sketch, "E174", {"start": v(673.1, 60.8) * mm, "mid": v(664.1, 51.8) * mm, "end": v(673.1, 42.8) * mm, "construction": true});
            skArc(sketch, "E175", {"start": v(673.1, 42.8) * mm, "mid": v(682.1, 51.8) * mm, "end": v(673.1, 60.8) * mm, "construction": true});
            skArc(sketch, "E176", {"start": v(513.1, 42.8) * mm, "mid": v(522.1, 51.8) * mm, "end": v(513.1, 60.8) * mm, "construction": true});
            skArc(sketch, "E177", {"start": v(513.1, 60.8) * mm, "mid": v(504.1, 51.8) * mm, "end": v(513.1, 42.8) * mm, "construction": true});
            skLineSegment(sketch, "E178.0", {"start": v(501.1, 39.8) * mm, "end": v(683.1, 39.8) * mm, "construction": true});
            skLineSegment(sketch, "E178.1", {"start": v(501.1, 188.8) * mm, "end": v(501.1, 39.8) * mm, "construction": true});
            skLineSegment(sketch, "E178.2", {"start": v(501.1, 188.8) * mm, "end": v(683.1, 188.8) * mm, "construction": true});
            skLineSegment(sketch, "E178.3", {"start": v(683.1, 188.8) * mm, "end": v(683.1, 39.8) * mm, "construction": true});
            skLineSegment(sketch, "E179", {"start": v(346.1, 166.8) * mm, "end": v(329.1, 166.8) * mm, "construction": true});
            skLineSegment(sketch, "E180", {"start": v(346.1, 149.8) * mm, "end": v(329.1, 149.8) * mm, "construction": true});
            skLineSegment(sketch, "E181", {"start": v(346.1, 76.8) * mm, "end": v(329.1, 76.8) * mm, "construction": true});
            skLineSegment(sketch, "E182", {"start": v(346.1, 59.8) * mm, "end": v(329.1, 59.8) * mm, "construction": true});
            skLineSegment(sketch, "E183", {"start": v(461.1, 59.8) * mm, "end": v(478.1, 59.8) * mm, "construction": true});
            skLineSegment(sketch, "E184", {"start": v(461.1, 76.8) * mm, "end": v(478.1, 76.8) * mm, "construction": true});
            skLineSegment(sketch, "E185", {"start": v(461.1, 149.8) * mm, "end": v(478.1, 149.8) * mm, "construction": true});
            skLineSegment(sketch, "E186", {"start": v(461.1, 166.8) * mm, "end": v(478.1, 166.8) * mm, "construction": true});
            skArc(sketch, "E187", {"start": v(346.1, 166.8) * mm, "mid": v(337.6, 158.3) * mm, "end": v(346.1, 149.8) * mm, "construction": true});
            skArc(sketch, "E188", {"start": v(346.1, 149.8) * mm, "mid": v(354.6, 158.3) * mm, "end": v(346.1, 166.8) * mm, "construction": true});
            skArc(sketch, "E189", {"start": v(461.1, 166.8) * mm, "mid": v(452.6, 158.3) * mm, "end": v(461.1, 149.8) * mm, "construction": true});
            skArc(sketch, "E190", {"start": v(461.1, 149.8) * mm, "mid": v(469.6, 158.3) * mm, "end": v(461.1, 166.8) * mm, "construction": true});
            skArc(sketch, "E191", {"start": v(461.1, 76.8) * mm, "mid": v(452.6, 68.3) * mm, "end": v(461.1, 59.8) * mm, "construction": true});
            skArc(sketch, "E192", {"start": v(461.1, 59.8) * mm, "mid": v(469.6, 68.3) * mm, "end": v(461.1, 76.8) * mm, "construction": true});
            skArc(sketch, "E193", {"start": v(346.1, 59.8) * mm, "mid": v(354.6, 68.3) * mm, "end": v(346.1, 76.8) * mm, "construction": true});
            skArc(sketch, "E194", {"start": v(346.1, 76.8) * mm, "mid": v(337.6, 68.3) * mm, "end": v(346.1, 59.8) * mm, "construction": true});
            skLineSegment(sketch, "E195.0", {"start": v(332.1, 171.3) * mm, "end": v(475.1, 171.3) * mm, "construction": true});
            skLineSegment(sketch, "E195.1", {"start": v(332.1, 171.3) * mm, "end": v(332.1, 57.3) * mm, "construction": true});
            skLineSegment(sketch, "E195.2", {"start": v(332.1, 57.3) * mm, "end": v(475.1, 57.3) * mm, "construction": true});
            skLineSegment(sketch, "E195.3", {"start": v(475.1, 171.3) * mm, "end": v(475.1, 57.3) * mm, "construction": true});
            skLineSegment(sketch, "E196", {"start": v(173.1, 193.8) * mm, "end": v(159.1, 193.8) * mm, "construction": true});
            skLineSegment(sketch, "E197", {"start": v(173.1, 175.8) * mm, "end": v(159.1, 175.8) * mm, "construction": true});
            skLineSegment(sketch, "E198", {"start": v(173.1, 53.8) * mm, "end": v(159.1, 53.8) * mm, "construction": true});
            skLineSegment(sketch, "E199", {"start": v(173.1, 35.8) * mm, "end": v(159.1, 35.8) * mm, "construction": true});
            skLineSegment(sketch, "E200", {"start": v(295.1, 193.8) * mm, "end": v(309.1, 193.8) * mm, "construction": true});
            skLineSegment(sketch, "E201", {"start": v(295.1, 175.8) * mm, "end": v(309.1, 175.8) * mm, "construction": true});
            skLineSegment(sketch, "E202", {"start": v(295.1, 83.8) * mm, "end": v(309.1, 83.8) * mm, "construction": true});
            skLineSegment(sketch, "E203", {"start": v(295.1, 65.8) * mm, "end": v(309.1, 65.8) * mm, "construction": true});
            skArc(sketch, "E204", {"start": v(173.1, 193.8) * mm, "mid": v(164.1, 184.8) * mm, "end": v(173.1, 175.8) * mm, "construction": true});
            skArc(sketch, "E205", {"start": v(173.1, 175.8) * mm, "mid": v(182.1, 184.8) * mm, "end": v(173.1, 193.8) * mm, "construction": true});
            skArc(sketch, "E206", {"start": v(173.1, 53.8) * mm, "mid": v(164.1, 44.8) * mm, "end": v(173.1, 35.8) * mm, "construction": true});
            skArc(sketch, "E207", {"start": v(173.1, 35.8) * mm, "mid": v(182.1, 44.8) * mm, "end": v(173.1, 53.8) * mm, "construction": true});
            skArc(sketch, "E208", {"start": v(295.1, 193.8) * mm, "mid": v(286.1, 184.8) * mm, "end": v(295.1, 175.8) * mm, "construction": true});
            skArc(sketch, "E209", {"start": v(295.1, 175.8) * mm, "mid": v(304.1, 184.8) * mm, "end": v(295.1, 193.8) * mm, "construction": true});
            skArc(sketch, "E210", {"start": v(295.1, 83.8) * mm, "mid": v(286.1, 74.8) * mm, "end": v(295.1, 65.8) * mm, "construction": true});
            skArc(sketch, "E211", {"start": v(295.1, 65.8) * mm, "mid": v(304.1, 74.8) * mm, "end": v(295.1, 83.8) * mm, "construction": true});
            skLineSegment(sketch, "E212.0", {"start": v(306.1, 62.8) * mm, "end": v(306.1, 198.8) * mm, "construction": true});
            skLineSegment(sketch, "E212.1", {"start": v(162.1, 198.8) * mm, "end": v(162.1, 29.8) * mm, "construction": true});
            skLineSegment(sketch, "E212.2", {"start": v(162.1, 29.8) * mm, "end": v(225.1, 29.8) * mm, "construction": true});
            skLineSegment(sketch, "E212.3", {"start": v(306.1, 198.8) * mm, "end": v(162.1, 198.8) * mm, "construction": true});
            skLineSegment(sketch, "E212.4", {"start": v(225.1, 62.8) * mm, "end": v(225.1, 29.8) * mm, "construction": true});
            skLineSegment(sketch, "E212.5", {"start": v(225.1, 62.8) * mm, "end": v(306.1, 62.8) * mm, "construction": true});
            skLineSegment(sketch, "E213", {"start": v(355.6, 231.78) * mm, "end": v(355.6, -3.17) * mm, "construction": true});
            skLineSegment(sketch, "E214.bottom", {"start": v(382.1, 11.83) * mm, "end": v(329.1, 11.83) * mm});
            skLineSegment(sketch, "E214.top", {"start": v(382.1, 31.83) * mm, "end": v(329.1, 31.83) * mm});
            skLineSegment(sketch, "E214.left", {"start": v(382.1, 11.83) * mm, "end": v(382.1, 31.83) * mm});
            skLineSegment(sketch, "E214.right", {"start": v(329.1, 11.83) * mm, "end": v(329.1, 31.83) * mm});
            skPoint(sketch, "E214.middle", {"position": v(355.6, 21.82) * mm});
            skCircle(sketch, "E215", {"center": v(38.1, 191.3) * mm, "radius": 7 * mm});
            skCircle(sketch, "E216", {"center": v(125.46, 191.3) * mm, "radius": 7 * mm});
            skCircle(sketch, "E217", {"center": v(38.1, 47.5) * mm, "radius": 7 * mm});
            skCircle(sketch, "E218", {"center": v(125.46, 47.5) * mm, "radius": 7 * mm});
            skCircle(sketch, "E219", {"center": v(113.46, 116.8) * mm, "radius": 11 * mm});
            skLineSegment(sketch, "E220", {"start": v(31.1, 191.3) * mm, "end": v(31.1, 47.5) * mm, "construction": true});
            skLineSegment(sketch, "E221", {"start": v(38.1, 198.3) * mm, "end": v(125.46, 198.3) * mm, "construction": true});
            skSolve(sketch);
        }
        {
            var Q0;
            Q0=makeQuery(id+"F5.imprint","IMPRINT",FACE,{"disambiguationData":[TD([[makeQuery(id+"F5.imprint","IMPRINT",EDGE,{"derivedFrom":sQuery(id+"F5.wireOp",EDGE,"E134.0.0")}),1.0]])]});
            var Q1;
            Q1=makeQuery(id+"F5.imprint","IMPRINT",FACE,{"disambiguationData":[TD([[makeQuery(id+"F5.imprint","IMPRINT",EDGE,{"derivedFrom":sQuery(id+"F5.wireOp",EDGE,"E134.0.0")}),-1.0]])]});
            var Q2;
            Q2=makeQuery(id+"F5.imprint","IMPRINT",FACE,{"disambiguationData":[TD([[makeQuery(id+"F5.imprint","IMPRINT",EDGE,{"derivedFrom":sQuery(id+"F5.wireOp",EDGE,"143005ec-1444-4292-adba-a346df852c2e")}),-1.0]])]});
            var Q3;
            Q3=makeQuery(id+"F5.imprint","IMPRINT",FACE,{"disambiguationData":[TD([[makeQuery(id+"F5.imprint","IMPRINT",EDGE,{"derivedFrom":sQuery(id+"F5.wireOp",EDGE,"37d7474f-1a28-43d0-ba76-85fe99742405")}),-1.0]])]});
            var Q4;
            Q4=makeQuery(id+"F5.imprint","IMPRINT",FACE,{"disambiguationData":[TD([[makeQuery(id+"F5.imprint","IMPRINT",EDGE,{"derivedFrom":sQuery(id+"F5.wireOp",EDGE,"e8dfdca3-3158-4d52-a5d6-508977a9ab62")}),-1.0]])]});
            var Q5;
            Q5=makeQuery(id+"F5.imprint","IMPRINT",FACE,{"disambiguationData":[TD([[makeQuery(id+"F5.imprint","IMPRINT",EDGE,{"derivedFrom":sQuery(id+"F5.wireOp",EDGE,"72282759-a10e-473f-8afb-279265fdd07c")}),-1.0]])]});
            var Q6;
            Q6=makeQuery(id+"F5.imprint","IMPRINT",FACE,{"disambiguationData":[TD([[makeQuery(id+"F5.imprint","IMPRINT",EDGE,{"derivedFrom":sQuery(id+"F5.wireOp",EDGE,"E147")}),-1.0]])]});
            var Q7;
            Q7=makeQuery(id+"F5.imprint","IMPRINT",FACE,{"disambiguationData":[TD([[makeQuery(id+"F5.imprint","IMPRINT",EDGE,{"derivedFrom":sQuery(id+"F5.wireOp",EDGE,"E145")}),-1.0]])]});
            var Q8;
            Q8=makeQuery(id+"F5.imprint","IMPRINT",FACE,{"disambiguationData":[TD([[makeQuery(id+"F5.imprint","IMPRINT",EDGE,{"derivedFrom":sQuery(id+"F5.wireOp",EDGE,"E146")}),-1.0]])]});
            var Q9;
            Q9=makeQuery(id+"F5.imprint","IMPRINT",FACE,{"disambiguationData":[TD([[makeQuery(id+"F5.imprint","IMPRINT",EDGE,{"derivedFrom":sQuery(id+"F5.wireOp",EDGE,"E148")}),-1.0]])]});
            var Q10;
            Q10=makeQuery(id+"F5.imprint","IMPRINT",FACE,{"disambiguationData":[TD([[makeQuery(id+"F5.imprint","IMPRINT",EDGE,{"derivedFrom":sQuery(id+"F5.wireOp",EDGE,"E152")}),-1.0]])]});
            var Q11;
            Q11=makeQuery(id+"F5.imprint","IMPRINT",FACE,{"disambiguationData":[TD([[makeQuery(id+"F5.imprint","IMPRINT",EDGE,{"derivedFrom":sQuery(id+"F5.wireOp",EDGE,"E155")}),-1.0]])]});
            var Q12;
            Q12=makeQuery(id+"F5.imprint","IMPRINT",FACE,{"disambiguationData":[TD([[makeQuery(id+"F5.imprint","IMPRINT",EDGE,{"derivedFrom":sQuery(id+"F5.wireOp",EDGE,"E154")}),-1.0]])]});
            var Q13;
            Q13=makeQuery(id+"F5.imprint","IMPRINT",FACE,{"disambiguationData":[TD([[makeQuery(id+"F5.imprint","IMPRINT",EDGE,{"derivedFrom":sQuery(id+"F5.wireOp",EDGE,"E153")}),-1.0]])]});
            var Q14;
            Q14=makeQuery(id+"F5.imprint","IMPRINT",FACE,{"disambiguationData":[TD([[makeQuery(id+"F5.imprint","IMPRINT",EDGE,{"derivedFrom":sQuery(id+"F5.wireOp",EDGE,"E158")}),-1.0]])]});
            var Q15;
            Q15=makeQuery(id+"F5.imprint","IMPRINT",FACE,{"disambiguationData":[TD([[makeQuery(id+"F5.imprint","IMPRINT",EDGE,{"derivedFrom":sQuery(id+"F5.wireOp",EDGE,"E161")}),-1.0]])]});
            var Q16;
            Q16=makeQuery(id+"F5.imprint","IMPRINT",FACE,{"disambiguationData":[TD([[makeQuery(id+"F5.imprint","IMPRINT",EDGE,{"derivedFrom":sQuery(id+"F5.wireOp",EDGE,"E159")}),-1.0]])]});
            var Q17;
            Q17=makeQuery(id+"F5.imprint","IMPRINT",FACE,{"disambiguationData":[TD([[makeQuery(id+"F5.imprint","IMPRINT",EDGE,{"derivedFrom":sQuery(id+"F5.wireOp",EDGE,"E160")}),-1.0]])]});
            extrude(context, id + "F6", {"entities" : qUnion([Q0, Q1, Q2, Q3, Q4, Q5, Q6, Q7, Q8, Q9, Q10, Q11, Q12, Q13, Q14, Q15, Q16, Q17]), "depth" : 3.17 * mm, "offsetDistance" : 25 * mm});
        }
    });
